# Revit family: Basin-One_Station-Acorn-Kurve®, Meridian-3791_Series
name_source: partatom
category: Plumbing Fixtures
units: mm (PartAtom-declared; Revit-internal decimal feet)

## family parameters
Cut with Voids When Loaded = No
Host = Face
OmniClass Number = 23.45.05.14.14
OmniClass Title = Sinks/Lavatories
Part Type = Normal
Room Calculation Point = No
Round Connector Dimension = Use Diameter
Shared = Yes

## types (2) — shared parameters
ADA Compliant = Yes
Assembly Code = D2010300
Bowl Shape = Curve
CW Connection = Yes
CWFU = 1.5
Compliance Certifications = Complies with IAPMO IGC 156, CSA B45 Series, ASME A112.18.1/CSA B125.1
Countertop, Basin and Sprayhead Shelf Material = Polymer Resin Corterra-Acorn-Solid Surface OCC11M
DV - Liquid / Lotion Soap Dispenser = Yes
Default Elevation = 34"
Description = One Station, Cast Solid Surface Kurve® Wash Basin
Faucet Material = Metal-Acorn-Stainless Steel
Flow Rate = 0.5 GPM
H - Hand Operation = No
HW Connection = Yes
HWFU = 1.5
Height = 21"
Inlet Connection Diameter = 1/2"
Inlet Connection Height = 21 1/2"
Installation Type = Wall Mounted
LWP - Less Waste Piping = No
Length = 24 5/8"
Manufacturer = Acorn
Material = Polymer Resin Corterra-Acorn-Solid Surface OCC11M
Operating Range = 30 PSI - 100 PSI
P-Trap Enclosure Material = Stainless Steel-Acorn-Satin
PPZ - Programmable Piezo Push button Electronic Metering = No
Product Documentation Link = https://www.acorneng.com
Product Page URL = https://www.acorneng.com
SO - Sensor Operated = No
SO-BAT- Sensor Operation (Batteries Not Included) = No
ST - Single Temperature Valve = No
Sensor Material = Plastic-Acorn-Black
URL = https://www.acorneng.com
Vent Connection = No
WFU = 2
Warranty Documentation Link = https://www.acorneng.com
Waste Connection = Yes
Waste Connection Diameter = 1 1/2"
Waste Connection Height = 25"
Width = 21"

## per-type parameters (varying)
| type | HW & CW Width | LO - Left Offset | Model Type | RO - Right Offset | Waste Connection Width |
| 3791-RO | 0" | No | Basin-One_Station-Acorn-Kurve®, Meridian-3791-RO : 3791-RO | Yes | 0" |
| 3791-LO | 8 1/2" | Yes | Basin-One_Station-Acorn-Kurve®, Meridian-3791-LO : 3791-LO | No | 3 1/2" |

note: column(s) folded — value = type name in every type: Model

## geometry (parser evidence)
native form markers: Sweep x11
no freeform markers — native parametric forms only
